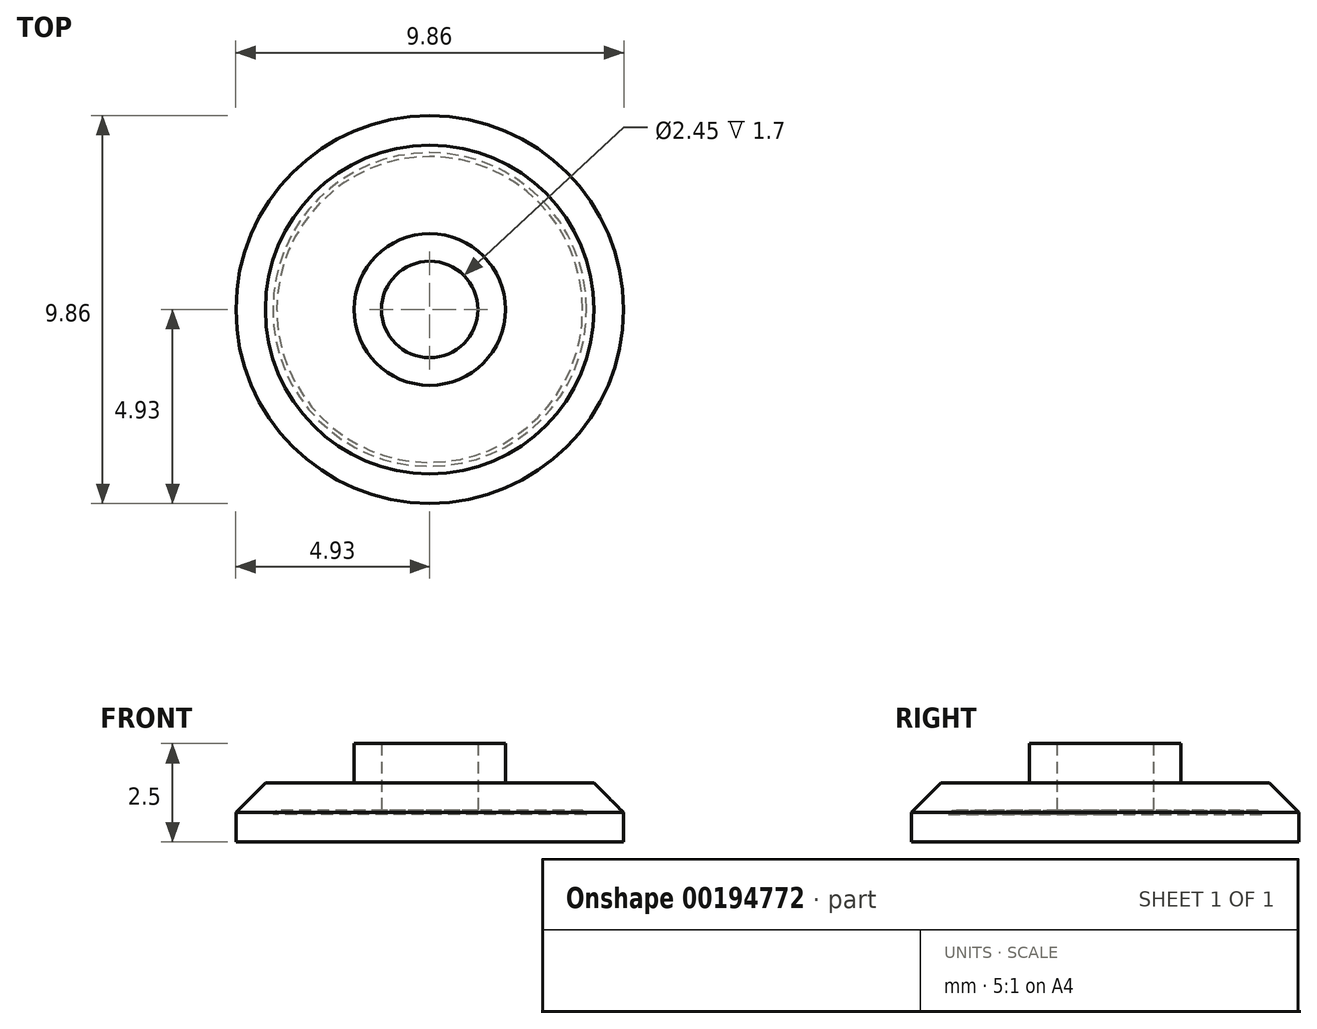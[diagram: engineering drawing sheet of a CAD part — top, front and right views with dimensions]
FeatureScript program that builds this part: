
annotation { "Feature Type Name" : "Feature", "Feature Type Description" : "" }
export const myFeature = defineFeature(function(context is Context, id is Id, definition is map)
    precondition{}
    {
        {
            var Q0;
            Q0=qCreatedBy(makeId("Top.planeOp"),FACE);
            var sketch = newSketch(context, id + "F0", { "sketchPlane" : qUnion([Q0])});
            skCircle(sketch, "E0", {"center": v(0, 0) * mm, "radius": 1.92 * mm});
            skCircle(sketch, "E1.0", {"center": v(0, 0) * mm, "radius": 4.93 * mm});
            skSolve(sketch);
        }
        {
            var Q0;
            Q0=makeQuery(id+"F0.imprint","IMPRINT",FACE,{"disambiguationData":[TD([[makeQuery(id+"F0.imprint","IMPRINT",EDGE,{"derivedFrom":sQuery(id+"F0.wireOp",EDGE,"E0")}),1.0]])]});
            extrude(context, id + "F1", {"entities" : qUnion([Q0]), "depth" : 1 * mm});
        }
        {
            var Q0;
            Q0=makeQuery(id+"F0.imprint","IMPRINT",FACE,{"disambiguationData":[TD([[makeQuery(id+"F0.imprint","IMPRINT",EDGE,{"derivedFrom":sQuery(id+"F0.wireOp",EDGE,"E0")}),-1.0]])]});
            var Q1;
            Q1=makeQuery(id+"F0.imprint","IMPRINT",FACE,{"disambiguationData":[TD([[makeQuery(id+"F0.imprint","IMPRINT",EDGE,{"derivedFrom":sQuery(id+"F0.wireOp",EDGE,"E0")}),1.0]])]});
            extrude(context, id + "F2", {"entities" : qUnion([Q0, Q1]), "operationType" : NewBodyOperationType.ADD, "oppositeDirection" : true, "depth" : 1.5 * mm});
        }
        {
            var Q0;
            Q0=makeQuery(id+"F2.opExtrude","CAP_EDGE",EDGE,{"disambiguationData":[OSD([sQuery(id+"F0.wireOp",EDGE,"E1.0")])],"isStart":true});
            chamfer(context, id + "F3", {"entities" : qUnion([Q0]), "width" : 0.75 * mm, "tangentPropagation" : true});
        }
        {
            var Q0;
            Q0=makeQuery(id+"F1.opExtrude","CAP_FACE",FACE,{"disambiguationData":[OSD([sQuery(id+"F0.wireOp",EDGE,"E0")])],"isStart":false});
            shell(context, id + "F4", {"entities" : qUnion([Q0]), "thickness" : 0.7 * mm});
        }
    });
